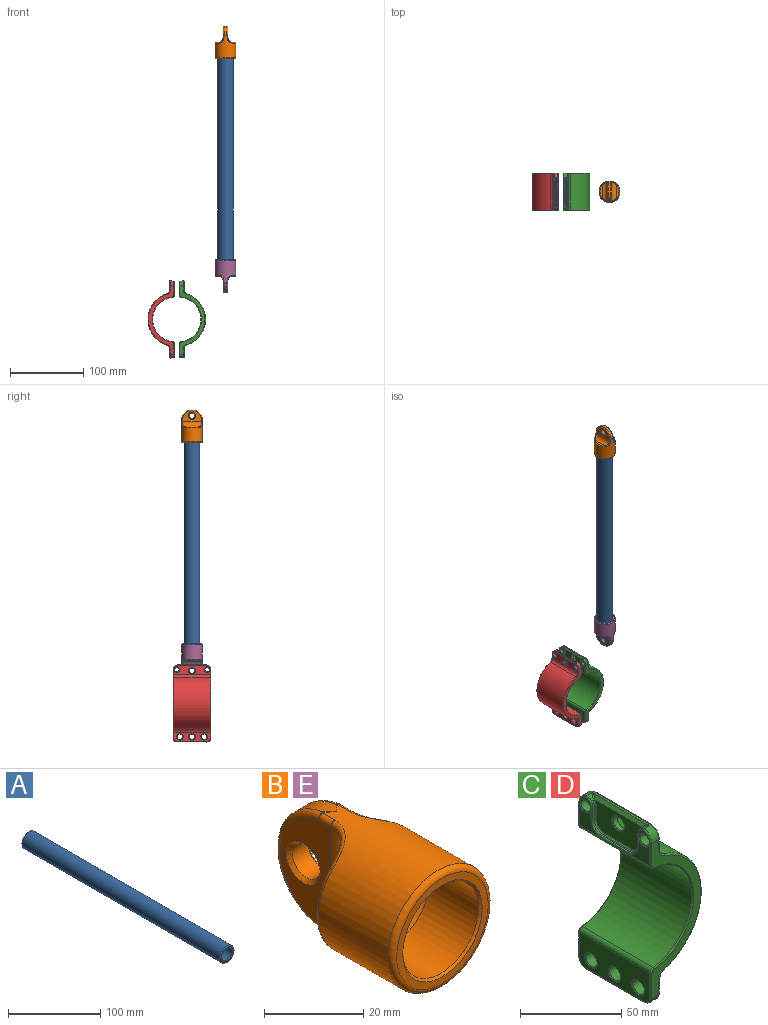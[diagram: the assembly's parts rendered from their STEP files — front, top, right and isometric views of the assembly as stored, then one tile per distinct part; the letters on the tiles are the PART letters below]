
ASSEMBLY  parts=5 mates=9
PART A: 8 faces, bbox 23.4x304.8x23.4 mm
  f0: cylinder r=7.94mm len=303.28mm, axis (0,1,0), area 15125.2mm2, adj f4,f5
  f1: cylinder r=10.79mm len=302.26mm, axis (0,1,0), area 20501.4mm2, adj f6,f7
  f2: plane 19.05x19.05mm, normal (0,-1,0), area 47.3mm2, adj f4,f7
  f3: plane 19.05x19.05mm, normal (0,1,0), area 47.3mm2, adj f5,f6
  f4: cone r=7.94mm half-angle=45deg, axis (0,-1,0), area 56.3mm2, adj f0,f2
  f5: cone r=8.7mm half-angle=45deg, axis (0,1,0), area 56.3mm2, adj f0,f3
  f6: torus R=9.53mm, axis (0,-1,0), area 129.5mm2, adj f1,f3
  f7: torus R=9.53mm, axis (0,-1,0), area 129.5mm2, adj f1,f2
PART B: 37 faces, bbox 30.9x45.6x30.9 mm
  f0: plane 25.75x14.61mm, normal (1,0,0), area 232.8mm2, adj f4,f17,f21,f23,f34
  f1: plane 25.75x14.61mm, normal (-1,0,0), area 232.8mm2, adj f7,f12,f16,f24,f29
  f2: cylinder r=14.29mm len=30.8mm, axis (0,1,0), area 1909.9mm2, adj f12,f13,f14,f15,f16,f17,f18,f19
  f3: plane 26.04x26.04mm, normal (0,-1,0), area 131mm2, adj f22,f25
  f4: cylinder r=6.35mm len=25.75mm, axis (0,0,1), area 236.8mm2, adj f0,f5,f18,f20
  f5: plane 17.75x3.49mm, normal (0,1,0), area 42.6mm2, adj f4,f19
  f6: plane 17.75x3.49mm, normal (0,1,0), area 42.6mm2, adj f7,f14
  f7: cylinder r=6.35mm len=25.75mm, axis (0,0,1), area 236.8mm2, adj f1,f6,f13,f15
  f8: cylinder r=10.79mm len=21.59mm, axis (0,-1,0), area 938.9mm2, adj f25,f26
  f9: plane 19.81x19.81mm, normal (0,-1,0), area 308.3mm2, adj f26
  f10: cylinder r=14.29mm len=28.58mm, axis (-1,0,0), area 163mm2, adj f27,f29,f30,f32,f34,f35
  f11: cylinder r=3.96mm len=7.92mm, axis (-1,0,0), area 113.8mm2, adj f23,f24
  f12: cylinder r=1.27mm len=3.49mm, axis (0,1,0), area 6.3mm2, adj f1,f2,f13,f28
  f13: bspline ~9.28x8.04mm, area 22mm2, adj f2,f7,f12,f14
  f14: torus R=13.02mm, axis (0,1,0), area 41.4mm2, adj f2,f6,f13,f15
  f15: bspline ~9.28x8.04mm, area 22mm2, adj f2,f7,f14,f16
  f16: cylinder r=1.27mm len=3.49mm, axis (0,1,0), area 6.3mm2, adj f1,f2,f15,f31
  f17: cylinder r=1.27mm len=3.49mm, axis (0,1,0), area 6.3mm2, adj f0,f2,f18,f33
  f18: bspline ~9.28x8.04mm, area 22mm2, adj f2,f4,f17,f19
  f19: torus R=13.02mm, axis (0,-1,0), area 41.4mm2, adj f2,f5,f18,f20
  f20: bspline ~9.29x9.28mm, area 22mm2, adj f2,f4,f19,f21
  f21: cylinder r=1.27mm len=3.49mm, axis (0,1,0), area 6.3mm2, adj f0,f2,f20,f36
  f22: torus R=13.02mm, axis (0,-1,0), area 173.3mm2, adj f2,f3
  f23: cone r=3.96mm half-angle=45deg, axis (1,0,0), area 34.8mm2, adj f0,f11
  f24: cone r=4.85mm half-angle=45deg, axis (-1,0,0), area 34.8mm2, adj f1,f11
  f25: cone r=10.79mm half-angle=45deg, axis (0,-1,0), area 49.9mm2, adj f3,f8
  f26: torus R=9.91mm, axis (0,-1,0), area 91.9mm2, adj f8,f9
  f27: bspline ~3.25x3.25mm, area 0.4mm2, adj f2,f10,f28
  f28: sphere r=1.27mm, area 0.2mm2, adj f12,f27,f29
  f29: torus R=13.02mm, axis (-1,0,0), area 78.5mm2, adj f1,f10,f28,f31
  f30: bspline ~3.25x3.25mm, area 0.4mm2, adj f2,f10,f31
  f31: sphere r=1.27mm, area 0.2mm2, adj f16,f29,f30
  f32: bspline ~3.25x3.25mm, area 0.4mm2, adj f2,f10,f33
  f33: sphere r=1.27mm, area 0.2mm2, adj f17,f32,f34
  f34: torus R=13.02mm, axis (-1,0,0), area 78.5mm2, adj f0,f10,f33,f36
  f35: bspline ~3.25x3.25mm, area 0.4mm2, adj f2,f10,f36
  f36: sphere r=1.27mm, area 0.2mm2, adj f21,f34,f35
PART C: 96 faces, bbox 39x51.9x105.9 mm
  f0: plane 49.28x19.17mm, normal (-1,0,0), area 748.2mm2, adj f6,f33,f35,f37,f39,f41,f76,f78
  f1: plane 49.28x11.94mm, normal (1,0,0), area 391.9mm2, adj f8,f55,f57,f59,f61,f63,f77,f79
  f2: plane 49.28x19.08mm, normal (-1,0,0), area 219.9mm2, adj f4,f32,f34,f36,f38,f40,f42,f44
  f3: cylinder r=6.35mm len=6.35mm, axis (1,0,0), area 44.6mm2, adj f12,f13,f22,f50,f60,f84,f85
  f4: cylinder r=2.54mm len=49.28mm, axis (0,-1,0), area 183.9mm2, adj f2,f5,f30,f47
  f5: cylinder r=30.16mm len=60.02mm, axis (0,-1,0), area 4368.7mm2, adj f4,f6,f29,f45
  f6: cylinder r=2.54mm len=49.28mm, axis (0,-1,0), area 183.9mm2, adj f0,f5,f31,f43
  f7: plane 40.64x4.83mm, normal (0,0,-1), area 196.1mm2, adj f27,f28,f37,f59
  f8: cylinder r=5.08mm len=49.28mm, axis (0,-1,0), area 318.7mm2, adj f1,f9,f53,f65
  f9: cylinder r=36.51mm len=69.82mm, axis (0,-1,0), area 4581.8mm2, adj f8,f10,f51,f66
  f10: cylinder r=5.08mm len=49.28mm, axis (0,-1,0), area 318.7mm2, adj f9,f11,f52,f64
  f11: plane 49.28x11.94mm, normal (1,0,0), area 420.9mm2, adj f10,f54,f56,f58,f60,f62,f68,f70
  f12: plane 38.1x1.27mm, normal (0,0,1), area 48.4mm2, adj f3,f15,f58,f83
  f13: plane 93.5x34.23mm, normal (0,1,0), area 605.9mm2, adj f3,f28,f41,f43,f45,f47,f49,f62
  f14: plane 93.5x34.23mm, normal (0,-1,0), area 605.9mm2, adj f15,f27,f29,f30,f31,f32,f33,f51
  f15: cylinder r=6.35mm len=6.35mm, axis (-1,0,0), area 44.6mm2, adj f12,f14,f21,f34,f56,f82,f91
  f16: plane 7.62x1.02mm, normal (0,1,0), area 7.7mm2, adj f17,f21,f38,f94
  f17: cylinder r=6.35mm len=6.35mm, axis (1,0,0), area 10.1mm2, adj f16,f18,f40,f92
  f18: plane 19.05x1.02mm, normal (0,0,1), area 19.4mm2, adj f17,f19,f42,f90
  f19: cylinder r=6.35mm len=6.35mm, axis (1,0,0), area 10.1mm2, adj f18,f20,f44,f89
  f20: plane 7.62x1.02mm, normal (0,-1,0), area 7.7mm2, adj f19,f22,f46,f88
  f21: cylinder r=5.08mm len=5mm, axis (1,0,0), area 11.6mm2, adj f15,f16,f36,f91,f93,f95
  f22: cylinder r=5.08mm len=5mm, axis (1,0,0), area 11.6mm2, adj f3,f20,f48,f85,f86,f87
  f23: plane 32.27x16.51mm, normal (-1,0,0), area 425mm2, adj f71,f83,f87,f88,f89,f90,f92,f94
  f24: cylinder r=3.96mm len=7.93mm, axis (1,0,0), area 69.6mm2, adj f71,f72
  f25: cylinder r=3.3mm len=6.6mm, axis (1,0,0), area 110.7mm2, adj f67,f68
  f26: cylinder r=3.3mm len=6.6mm, axis (1,0,0), area 110.7mm2, adj f69,f70
  f27: cylinder r=5.08mm len=5.08mm, axis (1,0,0), area 38.5mm2, adj f7,f14,f35,f57
  f28: cylinder r=5.08mm len=5.08mm, axis (-1,0,0), area 38.5mm2, adj f7,f13,f39,f61
  f29: torus R=30.92mm, axis (0,-1,0), area 107.1mm2, adj f5,f14,f30,f31
  f30: torus R=1.78mm, axis (0,-1,0), area 4mm2, adj f4,f14,f29,f32
  f31: torus R=1.78mm, axis (0,-1,0), area 4mm2, adj f6,f14,f29,f33
  f32: cylinder r=0.76mm len=13.58mm, axis (0,0,-1), area 16.3mm2, adj f2,f14,f30,f34
  f33: cylinder r=0.76mm len=14.85mm, axis (0,0,-1), area 17.8mm2, adj f0,f14,f31,f35
  f34: torus R=5.59mm, axis (1,0,0), area 10.2mm2, adj f2,f15,f32,f36
  f35: torus R=4.32mm, axis (-1,0,0), area 9mm2, adj f0,f27,f33,f37
  f36: torus R=4.32mm, axis (1,0,0), area 7.9mm2, adj f2,f21,f34,f38
  f37: cylinder r=0.76mm len=40.64mm, axis (0,-1,0), area 48.6mm2, adj f0,f7,f35,f39
  f38: cylinder r=0.76mm len=7.62mm, axis (0,0,-1), area 9.1mm2, adj f2,f16,f36,f40
  f39: torus R=4.32mm, axis (-1,0,0), area 9mm2, adj f0,f28,f37,f41
  f40: torus R=7.11mm, axis (1,0,0), area 12.5mm2, adj f2,f17,f38,f42
  f41: cylinder r=0.76mm len=14.85mm, axis (0,0,1), area 17.8mm2, adj f0,f13,f39,f43
  f42: cylinder r=0.76mm len=19.05mm, axis (0,1,0), area 22.8mm2, adj f2,f18,f40,f44
  f43: torus R=1.78mm, axis (0,-1,0), area 4mm2, adj f6,f13,f41,f45
  f44: torus R=7.11mm, axis (1,0,0), area 12.5mm2, adj f2,f19,f42,f46
  f45: torus R=30.92mm, axis (0,-1,0), area 107.1mm2, adj f5,f13,f43,f47
  f46: cylinder r=0.76mm len=7.62mm, axis (0,0,1), area 9.1mm2, adj f2,f20,f44,f48
  f47: torus R=1.78mm, axis (0,-1,0), area 4mm2, adj f4,f13,f45,f49
  f48: torus R=4.32mm, axis (1,0,0), area 7.9mm2, adj f2,f22,f46,f50
  f49: cylinder r=0.76mm len=13.58mm, axis (0,0,1), area 16.3mm2, adj f2,f13,f47,f50
  f50: torus R=5.59mm, axis (1,0,0), area 10.2mm2, adj f2,f3,f48,f49
  f51: torus R=35.75mm, axis (0,-1,0), area 110.5mm2, adj f9,f14,f52,f53
  f52: torus R=5.84mm, axis (0,-1,0), area 8.2mm2, adj f10,f14,f51,f54
  f53: torus R=5.84mm, axis (0,-1,0), area 8.2mm2, adj f8,f14,f51,f55
  f54: cylinder r=0.76mm len=6.35mm, axis (0,0,1), area 7.6mm2, adj f11,f14,f52,f56
  f55: cylinder r=0.76mm len=7.62mm, axis (0,0,1), area 9.1mm2, adj f1,f14,f53,f57
  f56: torus R=5.59mm, axis (-1,0,0), area 11.4mm2, adj f11,f15,f54,f58
  f57: torus R=4.32mm, axis (1,0,0), area 9mm2, adj f1,f27,f55,f59
  f58: cylinder r=0.76mm len=38.1mm, axis (0,-1,0), area 45.6mm2, adj f11,f12,f56,f60
  f59: cylinder r=0.76mm len=40.64mm, axis (0,-1,0), area 48.6mm2, adj f1,f7,f57,f61
  f60: torus R=5.59mm, axis (-1,0,0), area 11.4mm2, adj f3,f11,f58,f62
  f61: torus R=4.32mm, axis (1,0,0), area 9mm2, adj f1,f28,f59,f63
  f62: cylinder r=0.76mm len=6.35mm, axis (0,0,-1), area 7.6mm2, adj f11,f13,f60,f64
  f63: cylinder r=0.76mm len=7.62mm, axis (0,0,-1), area 9.1mm2, adj f1,f13,f61,f65
  f64: torus R=5.84mm, axis (0,-1,0), area 8.2mm2, adj f10,f13,f62,f66
  f65: torus R=5.84mm, axis (0,-1,0), area 8.2mm2, adj f8,f13,f63,f66
  f66: torus R=35.75mm, axis (0,-1,0), area 110.5mm2, adj f9,f13,f64,f65
  f67: cone r=3.81mm half-angle=45deg, axis (-1,0,0), area 16.1mm2, adj f2,f25
  f68: cone r=3.81mm half-angle=45deg, axis (1,0,0), area 16.1mm2, adj f11,f25
  f69: cone r=3.81mm half-angle=45deg, axis (-1,0,0), area 16.1mm2, adj f2,f26
  f70: cone r=3.81mm half-angle=45deg, axis (1,0,0), area 16.1mm2, adj f11,f26
  f71: cone r=4.47mm half-angle=45deg, axis (-1,0,0), area 19mm2, adj f23,f24
  f72: cone r=4.47mm half-angle=45deg, axis (1,0,0), area 19mm2, adj f11,f24
  f73: cylinder r=3.96mm len=7.93mm, axis (1,0,0), area 132.8mm2, adj f78,f79
  f74: cylinder r=3.96mm len=7.93mm, axis (1,0,0), area 132.8mm2, adj f80,f81
  f75: cylinder r=3.96mm len=7.93mm, axis (1,0,0), area 132.8mm2, adj f76,f77
  f76: cone r=4.47mm half-angle=45deg, axis (-1,0,0), area 19mm2, adj f0,f75
  f77: cone r=4.47mm half-angle=45deg, axis (1,0,0), area 19mm2, adj f1,f75
  f78: cone r=3.96mm half-angle=45deg, axis (-1,0,0), area 19mm2, adj f0,f73
  f79: cone r=3.96mm half-angle=45deg, axis (1,0,0), area 19mm2, adj f1,f73
  f80: cone r=3.96mm half-angle=45deg, axis (-1,0,0), area 19mm2, adj f0,f74
  f81: cone r=3.96mm half-angle=45deg, axis (1,0,0), area 19mm2, adj f1,f74
  f82: cone r=4.57mm half-angle=45deg, axis (1,0,0), area 0mm2, adj f15,f83,f91
  f83: plane 38.14x1.9mm, normal (-0.71,0,0.71), area 88.8mm2, adj f12,f23,f82,f84,f86,f87,f93,f95
  f84: cone r=4.57mm half-angle=45deg, axis (1,0,0), area 0mm2, adj f3,f83,f85
  f85: bspline ~2.4x1.37mm, area 0.4mm2, adj f3,f22,f84,f86
  f86: bspline ~2.93x2.44mm, area 2.6mm2, adj f22,f83,f85,f87
  f87: torus R=5.84mm, axis (1,0,0), area 4.1mm2, adj f22,f23,f83,f86,f88
  f88: cylinder r=0.76mm len=7.62mm, axis (0,0,-1), area 9.1mm2, adj f20,f23,f87,f89
  f89: torus R=5.59mm, axis (1,0,0), area 11.4mm2, adj f19,f23,f88,f90
  f90: cylinder r=0.76mm len=19.05mm, axis (0,-1,0), area 22.8mm2, adj f18,f23,f89,f92
  f91: bspline ~2.4x1.37mm, area 0.4mm2, adj f15,f21,f82,f93
  f92: torus R=5.59mm, axis (1,0,0), area 11.4mm2, adj f17,f23,f90,f94
  f93: bspline ~2.93x2.44mm, area 2.6mm2, adj f21,f83,f91,f95
  f94: cylinder r=0.76mm len=7.62mm, axis (0,0,1), area 9.1mm2, adj f16,f23,f92,f95
  f95: torus R=5.84mm, axis (1,0,0), area 4.1mm2, adj f21,f23,f83,f93,f94
PART D: same geometry as C
PART E: same geometry as B
PLACE A rot(axis=(-1,0,0),90deg) t=(258.99,-126.88,-73.01)mm
PLACE B rot(axis=(1,0,0),90deg) t=(258.99,-126.88,261)mm
PLACE C t=(195.38,-152.28,-138.82)mm
PLACE D rot(axis=(0,0,-1),180deg) t=(189.89,-101.48,-138.82)mm
PLACE E rot(axis=(-1,0,0),90deg) t=(258.99,-126.88,-102.22)mm
MATE cylindrical A.f1 <-> B.f8  axis (0,0,1) through (258.99,-126.88,230.52)mm
MATE fastened E.f8 <-> A.f1  axis (0,0,1) through (258.99,-126.88,-73.01)mm
MATE fastened B.f8 <-> A.f1  axis (0,0,-1) through (258.99,-126.88,231.79)mm
MATE cylindrical C.f24 <-> E.f11  axis (1,0,0) through (200.59,-126.88,-94.28)mm
MATE cylindrical E.f11 <-> D.f24  axis (-1,0,0) through (258.99,-126.88,-94.28)mm
MATE cylindrical D.f24 <-> E.f11  axis (-1,0,0) through (184.68,-126.88,-94.28)mm
MATE cylindrical A.f1 <-> E.f2  axis (0,0,-1) through (258.99,-126.88,-71.74)mm
MATE parallel B.f8 <-> A.f1  axis (0,0,-1) through (258.99,-126.88,231.79)mm
MATE cylindrical E.f11 <-> C.f24  axis (-1,0,0) through (258.99,-126.88,-94.28)mm
